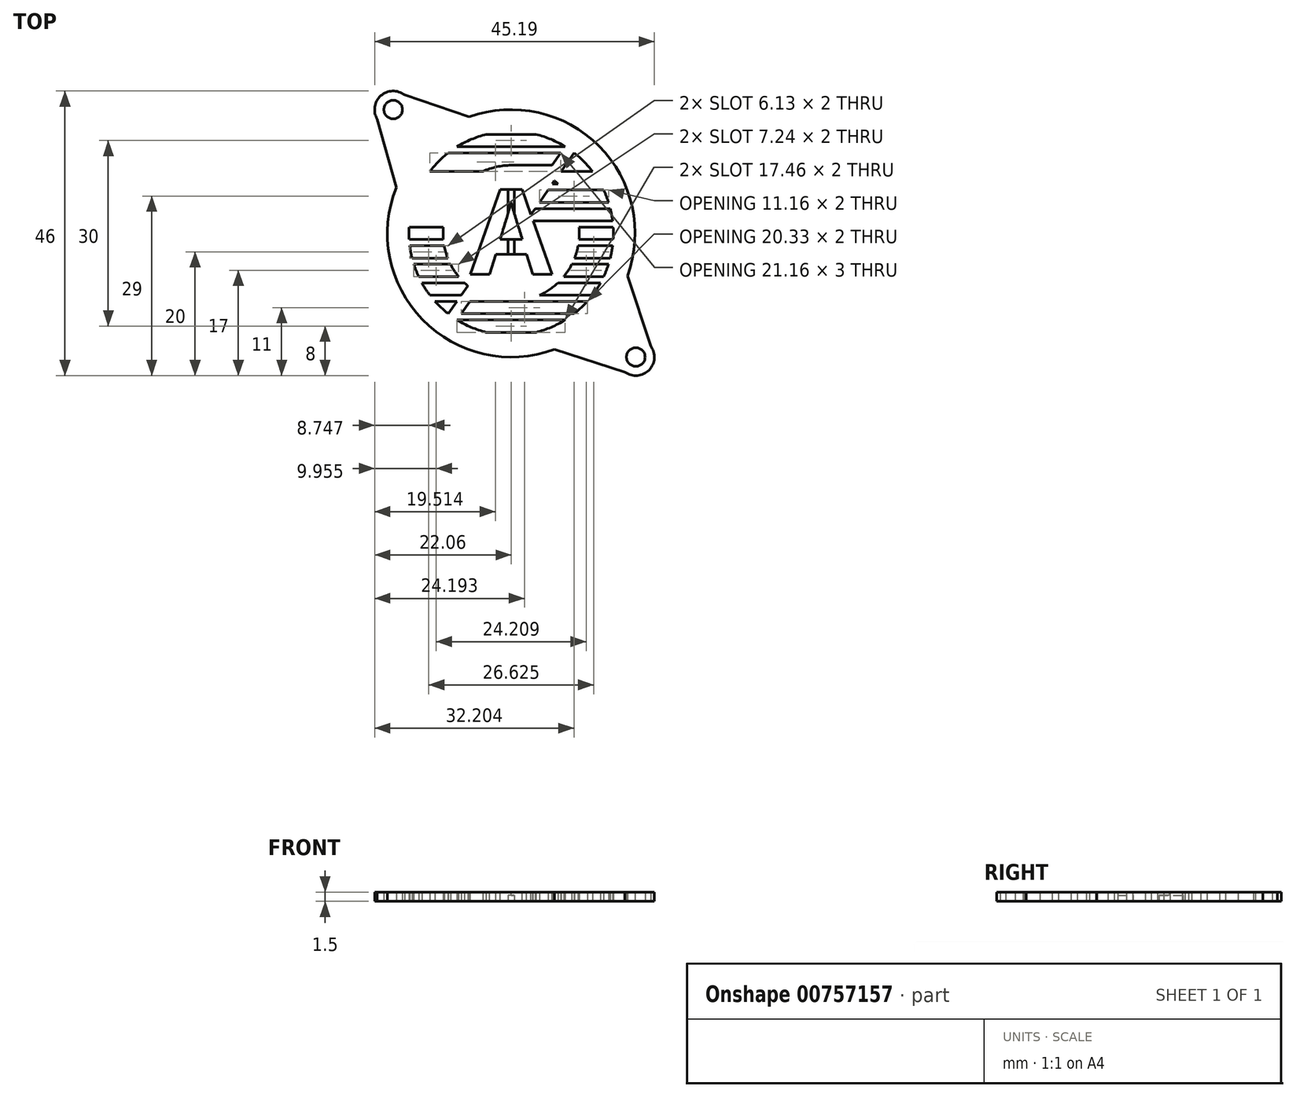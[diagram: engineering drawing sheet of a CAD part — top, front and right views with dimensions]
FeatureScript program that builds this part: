
annotation { "Feature Type Name" : "Feature", "Feature Type Description" : "" }
export const myFeature = defineFeature(function(context is Context, id is Id, definition is map)
    precondition{}
    {
        {
            var Q0;
            Q0=qCreatedBy(makeId("Top.planeOp"),FACE);
            var sketch = newSketch(context, id + "F0", { "sketchPlane" : qUnion([Q0])});
            skLineSegment(sketch, "E0", {"start": v(0, 0) * mm, "end": v(0, -20) * mm, "construction": true});
            skLineSegment(sketch, "E1", {"start": v(0, 0) * mm, "end": v(0, 20) * mm, "construction": true});
            skLineSegment(sketch, "E2", {"start": v(0, 20) * mm, "end": v(-19.06, 20) * mm, "construction": true});
            skLineSegment(sketch, "E3", {"start": v(0, -20) * mm, "end": v(20.13, -20) * mm, "construction": true});
            skCircle(sketch, "E4", {"center": v(-19.06, 20) * mm, "radius": 1.5 * mm});
            skCircle(sketch, "E5", {"center": v(20.13, -20) * mm, "radius": 1.5 * mm});
            skCircle(sketch, "E6", {"center": v(0, 0) * mm, "radius": 16.5 * mm});
            skArc(sketch, "E7", {"start": v(-17.23, 22.38) * mm, "mid": v(-21.06, 22.24) * mm, "end": v(-21.63, 18.45) * mm});
            skArc(sketch, "E8", {"start": v(18.38, -22.43) * mm, "mid": v(22.27, -22.1) * mm, "end": v(22.54, -18.2) * mm});
            skLineSegment(sketch, "E9", {"start": v(-19.06, 20) * mm, "end": v(-30.1, 20) * mm, "construction": true});
            skLineSegment(sketch, "E10", {"start": v(-19.06, 20) * mm, "end": v(-19.06, 32.46) * mm, "construction": true});
            skLineSegment(sketch, "E11", {"start": v(20.13, -20) * mm, "end": v(30, -20) * mm, "construction": true});
            skLineSegment(sketch, "E12", {"start": v(20.13, -20) * mm, "end": v(20.13, -30.36) * mm, "construction": true});
            skLineSegment(sketch, "E13", {"start": v(-21.63, 18.45) * mm, "end": v(-18.57, 7.43) * mm});
            skLineSegment(sketch, "E14", {"start": v(-17.23, 22.38) * mm, "end": v(-6.79, 18.81) * mm});
            skLineSegment(sketch, "E15", {"start": v(18.38, -22.43) * mm, "end": v(6.96, -18.75) * mm});
            skLineSegment(sketch, "E16", {"start": v(22.54, -18.2) * mm, "end": v(18.78, -6.88) * mm});
            skArc(sketch, "E17", {"start": v(-18.57, 7.43) * mm, "mid": v(-14.32, -13.96) * mm, "end": v(6.96, -18.75) * mm});
            skPoint(sketch, "E18.orphan", {"position": v(-16.5, 0) * mm});
            skPoint(sketch, "E19.orphan", {"position": v(16.5, 0) * mm});
            skArc(sketch, "E20.trimOffspring", {"start": v(18.78, -6.88) * mm, "mid": v(14.18, 14.1) * mm, "end": v(-6.79, 18.81) * mm});
            skLineSegment(sketch, "E21", {"start": v(-16.47, 1) * mm, "end": v(16.47, 1) * mm});
            skLineSegment(sketch, "E22", {"start": v(16.38, 2) * mm, "end": v(-16.38, 2) * mm});
            skLineSegment(sketch, "E23", {"start": v(-16, 4) * mm, "end": v(16, 4) * mm});
            skLineSegment(sketch, "E24", {"start": v(15.72, 5) * mm, "end": v(-15.72, 5) * mm});
            skLineSegment(sketch, "E25", {"start": v(-14.94, 7) * mm, "end": v(14.94, 7) * mm});
            skLineSegment(sketch, "E26", {"start": v(14.43, 8) * mm, "end": v(-14.43, 8) * mm});
            skLineSegment(sketch, "E27", {"start": v(-13.12, 10) * mm, "end": v(13.12, 10) * mm});
            skLineSegment(sketch, "E28", {"start": v(12.3, 11) * mm, "end": v(-12.3, 11) * mm});
            skLineSegment(sketch, "E29", {"start": v(-10.16, 13) * mm, "end": v(10.16, 13) * mm});
            skLineSegment(sketch, "E30", {"start": v(8.73, 14) * mm, "end": v(-8.73, 14) * mm});
            skLineSegment(sketch, "E31", {"start": v(-4.03, 16) * mm, "end": v(4.03, 16) * mm});
            skLineSegment(sketch, "E32.MirrorCS", {"start": v(-16.47, -1) * mm, "end": v(16.47, -1) * mm});
            skLineSegment(sketch, "E33.MirrorCS", {"start": v(16.38, -2) * mm, "end": v(-16.38, -2) * mm});
            skLineSegment(sketch, "E34.MirrorCS", {"start": v(-16, -4) * mm, "end": v(16, -4) * mm});
            skLineSegment(sketch, "E35.MirrorCS", {"start": v(15.72, -5) * mm, "end": v(-15.72, -5) * mm});
            skLineSegment(sketch, "E36.MirrorCS", {"start": v(-14.94, -7) * mm, "end": v(14.94, -7) * mm});
            skLineSegment(sketch, "E37.MirrorCS", {"start": v(14.43, -8) * mm, "end": v(-14.43, -8) * mm});
            skLineSegment(sketch, "E38.MirrorCS", {"start": v(-13.12, -10) * mm, "end": v(13.12, -10) * mm});
            skLineSegment(sketch, "E39.MirrorCS", {"start": v(12.3, -11) * mm, "end": v(-12.3, -11) * mm});
            skLineSegment(sketch, "E40.MirrorCS", {"start": v(-10.16, -13) * mm, "end": v(10.16, -13) * mm});
            skLineSegment(sketch, "E41.MirrorCS", {"start": v(-4.03, -16) * mm, "end": v(4.03, -16) * mm});
            skLineSegment(sketch, "E42.MirrorCS", {"start": v(8.73, -14) * mm, "end": v(-8.73, -14) * mm});
            skLineSegment(sketch, "E43", {"start": v(8.73, 14) * mm, "end": v(-10.16, -13) * mm});
            skLineSegment(sketch, "E44", {"start": v(-8.73, -14) * mm, "end": v(10.16, 13) * mm});
            skCircle(sketch, "E45", {"center": v(0, 0) * mm, "radius": 11 * mm});
            skSolve(sketch);
        }
        {
            var Q0;
            Q0=makeQuery(id+"F0.imprint","IMPRINT",FACE,{"disambiguationData":[TD([[makeQuery(id+"F0.imprint","IMPRINT",EDGE,{"derivedFrom":sQuery(id+"F0.wireOp",EDGE,"E4")}),-1.0]])]});
            extrude(context, id + "F1", {"entities" : qUnion([Q0]), "depth" : 1.5 * mm, "offsetDistance" : 25 * mm});
        }
        {
            var Q0;
            {var subQ0=sQuery(id+"F0.wireOp",EDGE,"E31");Q0=makeQuery(id+"F0.imprint","IMPRINT",FACE,{"disambiguationData":[TD([[makeQuery(id+"F0.imprint","IMPRINT",EDGE,{"derivedFrom":subQ0}),1.0]])]});}
            var Q1;
            {var subQ0=sQuery(id+"F0.wireOp",EDGE,"E29");Q1=makeQuery(id+"F0.imprint","IMPRINT",FACE,{"disambiguationData":[TD([[makeQuery(id+"F0.imprint","IMPRINT",EDGE,{"derivedFrom":subQ0}),1.0]])]});}
            var Q2;
            {var subQ0=sQuery(id+"F0.wireOp",EDGE,"E27");Q2=makeQuery(id+"F0.imprint","IMPRINT",FACE,{"disambiguationData":[TD([[makeQuery(id+"F0.imprint","IMPRINT",EDGE,{"derivedFrom":subQ0}),1.0]])]});}
            var Q3;
            {var subQ0=sQuery(id+"F0.wireOp",EDGE,"E25");Q3=makeQuery(id+"F0.imprint","IMPRINT",FACE,{"disambiguationData":[TD([[makeQuery(id+"F0.imprint","IMPRINT",EDGE,{"derivedFrom":subQ0}),1.0]])]});}
            var Q4;
            {var subQ0=sQuery(id+"F0.wireOp",EDGE,"E23");Q4=makeQuery(id+"F0.imprint","IMPRINT",FACE,{"disambiguationData":[TD([[makeQuery(id+"F0.imprint","IMPRINT",EDGE,{"derivedFrom":subQ0}),1.0]])]});}
            var Q5;
            {var subQ0=sQuery(id+"F0.wireOp",EDGE,"E21");Q5=makeQuery(id+"F0.imprint","IMPRINT",FACE,{"disambiguationData":[TD([[makeQuery(id+"F0.imprint","IMPRINT",EDGE,{"derivedFrom":subQ0}),1.0]])]});}
            var Q6;
            {var subQ0=sQuery(id+"F0.wireOp",EDGE,"E32.MirrorCS");Q6=makeQuery(id+"F0.imprint","IMPRINT",FACE,{"disambiguationData":[TD([[makeQuery(id+"F0.imprint","IMPRINT",EDGE,{"derivedFrom":subQ0}),-1.0]])]});}
            var Q7;
            {var subQ0=sQuery(id+"F0.wireOp",EDGE,"E34.MirrorCS");Q7=makeQuery(id+"F0.imprint","IMPRINT",FACE,{"disambiguationData":[TD([[makeQuery(id+"F0.imprint","IMPRINT",EDGE,{"derivedFrom":subQ0}),-1.0]])]});}
            var Q8;
            {var subQ0=sQuery(id+"F0.wireOp",EDGE,"E36.MirrorCS");Q8=makeQuery(id+"F0.imprint","IMPRINT",FACE,{"disambiguationData":[TD([[makeQuery(id+"F0.imprint","IMPRINT",EDGE,{"derivedFrom":subQ0}),-1.0]])]});}
            var Q9;
            {var subQ0=sQuery(id+"F0.wireOp",EDGE,"E38.MirrorCS");Q9=makeQuery(id+"F0.imprint","IMPRINT",FACE,{"disambiguationData":[TD([[makeQuery(id+"F0.imprint","IMPRINT",EDGE,{"derivedFrom":subQ0}),-1.0]])]});}
            var Q10;
            {var subQ0=sQuery(id+"F0.wireOp",EDGE,"E40.MirrorCS");Q10=makeQuery(id+"F0.imprint","IMPRINT",FACE,{"disambiguationData":[TD([[makeQuery(id+"F0.imprint","IMPRINT",EDGE,{"derivedFrom":subQ0}),-1.0]])]});}
            var Q11;
            {var subQ0=sQuery(id+"F0.wireOp",EDGE,"E41.MirrorCS");Q11=makeQuery(id+"F0.imprint","IMPRINT",FACE,{"disambiguationData":[TD([[makeQuery(id+"F0.imprint","IMPRINT",EDGE,{"derivedFrom":subQ0}),-1.0]])]});}
            var Q12;
            {var subQ3=sQuery(id+"F0.wireOp",EDGE,"E42.MirrorCS");Q12=makeQuery(id+"F0.imprint","IMPRINT",FACE,{"disambiguationData":[TD([[makeQuery(id+"F0.imprint","IMPRINT",EDGE,{"derivedFrom":subQ3}),-1.0]])]});}
            var Q13;
            {var subQ3=sQuery(id+"F0.wireOp",EDGE,"E30");Q13=makeQuery(id+"F0.imprint","IMPRINT",FACE,{"disambiguationData":[TD([[makeQuery(id+"F0.imprint","IMPRINT",EDGE,{"derivedFrom":subQ3}),1.0]])]});}
            var Q14;
            {var subQ0=sQuery(id+"F0.wireOp",EDGE,"E44");var subQ1=sQuery(id+"F0.wireOp",EDGE,"E39.MirrorCS");var subQ2=makeQuery(id+"F0.imprint","INTERSECT",VERTEX,{"derivedFrom":[subQ1,subQ0]});Q14=makeQuery(id+"F0.imprint","IMPRINT",FACE,{"disambiguationData":[TD([[makeQuery(id+"F0.imprint","IMPRINT",EDGE,{"disambiguationData":[TD([[subQ2,-1.0]])],"derivedFrom":subQ1}),1.0]])]});}
            var Q15;
            {var subQ0=sQuery(id+"F0.wireOp",EDGE,"E44");var subQ1=sQuery(id+"F0.wireOp",EDGE,"E37.MirrorCS");var subQ2=makeQuery(id+"F0.imprint","INTERSECT",VERTEX,{"derivedFrom":[subQ1,subQ0]});Q15=makeQuery(id+"F0.imprint","IMPRINT",FACE,{"disambiguationData":[TD([[makeQuery(id+"F0.imprint","IMPRINT",EDGE,{"disambiguationData":[TD([[subQ2,-1.0]])],"derivedFrom":subQ1}),1.0]])]});}
            var Q16;
            {var subQ0=sQuery(id+"F0.wireOp",EDGE,"E44");var subQ1=sQuery(id+"F0.wireOp",EDGE,"E35.MirrorCS");var subQ2=makeQuery(id+"F0.imprint","INTERSECT",VERTEX,{"derivedFrom":[subQ1,subQ0]});Q16=makeQuery(id+"F0.imprint","IMPRINT",FACE,{"disambiguationData":[TD([[makeQuery(id+"F0.imprint","IMPRINT",EDGE,{"disambiguationData":[TD([[subQ2,-1.0]])],"derivedFrom":subQ1}),1.0]])]});}
            var Q17;
            {var subQ0=sQuery(id+"F0.wireOp",EDGE,"E44");var subQ1=sQuery(id+"F0.wireOp",EDGE,"E33.MirrorCS");var subQ2=makeQuery(id+"F0.imprint","INTERSECT",VERTEX,{"derivedFrom":[subQ1,subQ0]});Q17=makeQuery(id+"F0.imprint","IMPRINT",FACE,{"disambiguationData":[TD([[makeQuery(id+"F0.imprint","IMPRINT",EDGE,{"disambiguationData":[TD([[subQ2,-1.0]])],"derivedFrom":subQ1}),1.0]])]});}
            var Q18;
            {var subQ0=sQuery(id+"F0.wireOp",EDGE,"E43");var subQ1=sQuery(id+"F0.wireOp",EDGE,"E21");var subQ2=makeQuery(id+"F0.imprint","INTERSECT",VERTEX,{"derivedFrom":[subQ1,subQ0]});Q18=makeQuery(id+"F0.imprint","IMPRINT",FACE,{"disambiguationData":[TD([[makeQuery(id+"F0.imprint","IMPRINT",EDGE,{"disambiguationData":[TD([[subQ2,-1.0]])],"derivedFrom":subQ1}),-1.0]])]});}
            var Q19;
            {var subQ0=sQuery(id+"F0.wireOp",EDGE,"E44");var subQ1=sQuery(id+"F0.wireOp",EDGE,"E22");var subQ2=makeQuery(id+"F0.imprint","INTERSECT",VERTEX,{"derivedFrom":[subQ1,subQ0]});Q19=makeQuery(id+"F0.imprint","IMPRINT",FACE,{"disambiguationData":[TD([[makeQuery(id+"F0.imprint","IMPRINT",EDGE,{"disambiguationData":[TD([[subQ2,-1.0]])],"derivedFrom":subQ1}),-1.0]])]});}
            var Q20;
            {var subQ0=sQuery(id+"F0.wireOp",EDGE,"E44");var subQ1=sQuery(id+"F0.wireOp",EDGE,"E24");var subQ2=makeQuery(id+"F0.imprint","INTERSECT",VERTEX,{"derivedFrom":[subQ1,subQ0]});Q20=makeQuery(id+"F0.imprint","IMPRINT",FACE,{"disambiguationData":[TD([[makeQuery(id+"F0.imprint","IMPRINT",EDGE,{"disambiguationData":[TD([[subQ2,-1.0]])],"derivedFrom":subQ1}),-1.0]])]});}
            var Q21;
            {var subQ0=sQuery(id+"F0.wireOp",EDGE,"E44");var subQ1=sQuery(id+"F0.wireOp",EDGE,"E26");var subQ2=makeQuery(id+"F0.imprint","INTERSECT",VERTEX,{"derivedFrom":[subQ1,subQ0]});Q21=makeQuery(id+"F0.imprint","IMPRINT",FACE,{"disambiguationData":[TD([[makeQuery(id+"F0.imprint","IMPRINT",EDGE,{"disambiguationData":[TD([[subQ2,-1.0]])],"derivedFrom":subQ1}),-1.0]])]});}
            var Q22;
            {var subQ0=sQuery(id+"F0.wireOp",EDGE,"E44");var subQ1=sQuery(id+"F0.wireOp",EDGE,"E28");var subQ2=makeQuery(id+"F0.imprint","INTERSECT",VERTEX,{"derivedFrom":[subQ1,subQ0]});Q22=makeQuery(id+"F0.imprint","IMPRINT",FACE,{"disambiguationData":[TD([[makeQuery(id+"F0.imprint","IMPRINT",EDGE,{"disambiguationData":[TD([[subQ2,-1.0]])],"derivedFrom":subQ1}),-1.0]])]});}
            var Q23;
            {var subQ0=sQuery(id+"F0.wireOp",EDGE,"E43");var subQ1=sQuery(id+"F0.wireOp",EDGE,"E26");var subQ2=makeQuery(id+"F0.imprint","INTERSECT",VERTEX,{"derivedFrom":[subQ1,subQ0]});Q23=makeQuery(id+"F0.imprint","IMPRINT",FACE,{"disambiguationData":[TD([[makeQuery(id+"F0.imprint","IMPRINT",EDGE,{"disambiguationData":[TD([[subQ2,-1.0]])],"derivedFrom":subQ1}),-1.0]])]});}
            var Q24;
            {var subQ0=sQuery(id+"F0.wireOp",EDGE,"E43");var subQ1=sQuery(id+"F0.wireOp",EDGE,"E24");var subQ2=makeQuery(id+"F0.imprint","INTERSECT",VERTEX,{"derivedFrom":[subQ1,subQ0]});Q24=makeQuery(id+"F0.imprint","IMPRINT",FACE,{"disambiguationData":[TD([[makeQuery(id+"F0.imprint","IMPRINT",EDGE,{"disambiguationData":[TD([[subQ2,-1.0]])],"derivedFrom":subQ1}),-1.0]])]});}
            var Q25;
            {var subQ0=sQuery(id+"F0.wireOp",EDGE,"E43");var subQ1=sQuery(id+"F0.wireOp",EDGE,"E27");var subQ2=makeQuery(id+"F0.imprint","INTERSECT",VERTEX,{"derivedFrom":[subQ1,subQ0]});Q25=makeQuery(id+"F0.imprint","IMPRINT",FACE,{"disambiguationData":[TD([[makeQuery(id+"F0.imprint","IMPRINT",EDGE,{"disambiguationData":[TD([[subQ2,-1.0]])],"derivedFrom":subQ1}),-1.0]])]});}
            var Q26;
            {var subQ0=sQuery(id+"F0.wireOp",EDGE,"E43");var subQ1=sQuery(id+"F0.wireOp",EDGE,"E27");var subQ2=makeQuery(id+"F0.imprint","INTERSECT",VERTEX,{"derivedFrom":[subQ1,subQ0]});Q26=makeQuery(id+"F0.imprint","IMPRINT",FACE,{"disambiguationData":[TD([[makeQuery(id+"F0.imprint","IMPRINT",EDGE,{"disambiguationData":[TD([[subQ2,-1.0]])],"derivedFrom":subQ1}),1.0]])]});}
            var Q27;
            {var subQ0=sQuery(id+"F0.wireOp",EDGE,"E45");var subQ1=sQuery(id+"F0.wireOp",EDGE,"E27");var subQ2=makeQuery(id+"F0.imprint","INTERSECT",VERTEX,{"disambiguationData":[OD(1.0)],"derivedFrom":[subQ1,subQ0]});Q27=makeQuery(id+"F0.imprint","IMPRINT",FACE,{"disambiguationData":[TD([[makeQuery(id+"F0.imprint","IMPRINT",EDGE,{"disambiguationData":[TD([[subQ2,-1.0]])],"derivedFrom":subQ1}),1.0]])]});}
            var Q28;
            {var subQ0=sQuery(id+"F0.wireOp",EDGE,"E27");var subQ1=sQuery(id+"F0.wireOp",EDGE,"E6");var subQ2=makeQuery(id+"F0.imprint","INTERSECT",VERTEX,{"disambiguationData":[OD(1.0)],"derivedFrom":[subQ1,subQ0]});Q28=makeQuery(id+"F0.imprint","IMPRINT",FACE,{"disambiguationData":[TD([[makeQuery(id+"F0.imprint","IMPRINT",EDGE,{"disambiguationData":[TD([[subQ2,-1.0]])],"derivedFrom":subQ1}),1.0]])]});}
            var Q29;
            {var subQ0=sQuery(id+"F0.wireOp",EDGE,"E27");var subQ1=sQuery(id+"F0.wireOp",EDGE,"E6");var subQ2=makeQuery(id+"F0.imprint","INTERSECT",VERTEX,{"disambiguationData":[OD(0.0)],"derivedFrom":[subQ1,subQ0]});Q29=makeQuery(id+"F0.imprint","IMPRINT",FACE,{"disambiguationData":[TD([[makeQuery(id+"F0.imprint","IMPRINT",EDGE,{"disambiguationData":[TD([[subQ2,1.0]])],"derivedFrom":subQ1}),1.0]])]});}
            var Q30;
            {var subQ0=sQuery(id+"F0.wireOp",EDGE,"E38.MirrorCS");var subQ1=sQuery(id+"F0.wireOp",EDGE,"E6");var subQ2=makeQuery(id+"F0.imprint","INTERSECT",VERTEX,{"disambiguationData":[OD(0.0)],"derivedFrom":[subQ1,subQ0]});Q30=makeQuery(id+"F0.imprint","IMPRINT",FACE,{"disambiguationData":[TD([[makeQuery(id+"F0.imprint","IMPRINT",EDGE,{"disambiguationData":[TD([[subQ2,-1.0]])],"derivedFrom":subQ1}),1.0]])]});}
            var Q31;
            {var subQ0=sQuery(id+"F0.wireOp",EDGE,"E43");var subQ1=sQuery(id+"F0.wireOp",EDGE,"E38.MirrorCS");var subQ2=makeQuery(id+"F0.imprint","INTERSECT",VERTEX,{"derivedFrom":[subQ1,subQ0]});Q31=makeQuery(id+"F0.imprint","IMPRINT",FACE,{"disambiguationData":[TD([[makeQuery(id+"F0.imprint","IMPRINT",EDGE,{"disambiguationData":[TD([[subQ2,-1.0]])],"derivedFrom":subQ1}),-1.0]])]});}
            var Q32;
            {var subQ0=sQuery(id+"F0.wireOp",EDGE,"E43");var subQ1=sQuery(id+"F0.wireOp",EDGE,"E38.MirrorCS");var subQ2=makeQuery(id+"F0.imprint","INTERSECT",VERTEX,{"derivedFrom":[subQ1,subQ0]});Q32=makeQuery(id+"F0.imprint","IMPRINT",FACE,{"disambiguationData":[TD([[makeQuery(id+"F0.imprint","IMPRINT",EDGE,{"disambiguationData":[TD([[subQ2,-1.0]])],"derivedFrom":subQ1}),1.0]])]});}
            var Q33;
            {var subQ0=sQuery(id+"F0.wireOp",EDGE,"E44");var subQ1=sQuery(id+"F0.wireOp",EDGE,"E38.MirrorCS");var subQ2=makeQuery(id+"F0.imprint","INTERSECT",VERTEX,{"derivedFrom":[subQ1,subQ0]});Q33=makeQuery(id+"F0.imprint","IMPRINT",FACE,{"disambiguationData":[TD([[makeQuery(id+"F0.imprint","IMPRINT",EDGE,{"disambiguationData":[TD([[subQ2,-1.0]])],"derivedFrom":subQ1}),-1.0]])]});}
            var Q34;
            {var subQ0=sQuery(id+"F0.wireOp",EDGE,"E38.MirrorCS");var subQ1=sQuery(id+"F0.wireOp",EDGE,"E6");var subQ2=makeQuery(id+"F0.imprint","INTERSECT",VERTEX,{"disambiguationData":[OD(1.0)],"derivedFrom":[subQ1,subQ0]});Q34=makeQuery(id+"F0.imprint","IMPRINT",FACE,{"disambiguationData":[TD([[makeQuery(id+"F0.imprint","IMPRINT",EDGE,{"disambiguationData":[TD([[subQ2,1.0]])],"derivedFrom":subQ1}),1.0]])]});}
            var Q35;
            {var subQ0=sQuery(id+"F0.wireOp",EDGE,"E45");var subQ5=sQuery(id+"F0.wireOp",EDGE,"E37.MirrorCS");var subQ8=makeQuery(id+"F0.imprint","INTERSECT",VERTEX,{"disambiguationData":[OD(0.0)],"derivedFrom":[subQ5,subQ0]});Q35=makeQuery(id+"F0.imprint","IMPRINT",FACE,{"disambiguationData":[TD([[makeQuery(id+"F0.imprint","IMPRINT",EDGE,{"disambiguationData":[TD([[subQ8,-1.0]])],"derivedFrom":subQ5}),1.0]])]});}
            var Q36;
            {var subQ0=sQuery(id+"F0.wireOp",EDGE,"E45");var subQ1=sQuery(id+"F0.wireOp",EDGE,"E35.MirrorCS");var subQ2=makeQuery(id+"F0.imprint","INTERSECT",VERTEX,{"disambiguationData":[OD(0.0)],"derivedFrom":[subQ1,subQ0]});Q36=makeQuery(id+"F0.imprint","IMPRINT",FACE,{"disambiguationData":[TD([[makeQuery(id+"F0.imprint","IMPRINT",EDGE,{"disambiguationData":[TD([[subQ2,-1.0]])],"derivedFrom":subQ1}),1.0]])]});}
            var Q37;
            {var subQ0=sQuery(id+"F0.wireOp",EDGE,"E45");var subQ1=sQuery(id+"F0.wireOp",EDGE,"E33.MirrorCS");var subQ2=makeQuery(id+"F0.imprint","INTERSECT",VERTEX,{"disambiguationData":[OD(0.0)],"derivedFrom":[subQ1,subQ0]});Q37=makeQuery(id+"F0.imprint","IMPRINT",FACE,{"disambiguationData":[TD([[makeQuery(id+"F0.imprint","IMPRINT",EDGE,{"disambiguationData":[TD([[subQ2,-1.0]])],"derivedFrom":subQ1}),1.0]])]});}
            var Q38;
            {var subQ0=sQuery(id+"F0.wireOp",EDGE,"E44");var subQ1=sQuery(id+"F0.wireOp",EDGE,"E21");var subQ2=makeQuery(id+"F0.imprint","INTERSECT",VERTEX,{"derivedFrom":[subQ1,subQ0]});Q38=makeQuery(id+"F0.imprint","IMPRINT",FACE,{"disambiguationData":[TD([[makeQuery(id+"F0.imprint","IMPRINT",EDGE,{"disambiguationData":[TD([[subQ2,-1.0]])],"derivedFrom":subQ1}),-1.0]])]});}
            var Q39;
            {var subQ0=sQuery(id+"F0.wireOp",EDGE,"E45");var subQ1=sQuery(id+"F0.wireOp",EDGE,"E22");var subQ2=makeQuery(id+"F0.imprint","INTERSECT",VERTEX,{"disambiguationData":[OD(0.0)],"derivedFrom":[subQ1,subQ0]});Q39=makeQuery(id+"F0.imprint","IMPRINT",FACE,{"disambiguationData":[TD([[makeQuery(id+"F0.imprint","IMPRINT",EDGE,{"disambiguationData":[TD([[subQ2,-1.0]])],"derivedFrom":subQ1}),-1.0]])]});}
            var Q40;
            {var subQ0=sQuery(id+"F0.wireOp",EDGE,"E45");var subQ1=sQuery(id+"F0.wireOp",EDGE,"E24");var subQ2=makeQuery(id+"F0.imprint","INTERSECT",VERTEX,{"disambiguationData":[OD(0.0)],"derivedFrom":[subQ1,subQ0]});Q40=makeQuery(id+"F0.imprint","IMPRINT",FACE,{"disambiguationData":[TD([[makeQuery(id+"F0.imprint","IMPRINT",EDGE,{"disambiguationData":[TD([[subQ2,-1.0]])],"derivedFrom":subQ1}),-1.0]])]});}
            var Q41;
            {var subQ0=sQuery(id+"F0.wireOp",EDGE,"E43");var subQ1=sQuery(id+"F0.wireOp",EDGE,"E22");var subQ2=makeQuery(id+"F0.imprint","INTERSECT",VERTEX,{"derivedFrom":[subQ1,subQ0]});Q41=makeQuery(id+"F0.imprint","IMPRINT",FACE,{"disambiguationData":[TD([[makeQuery(id+"F0.imprint","IMPRINT",EDGE,{"disambiguationData":[TD([[subQ2,-1.0]])],"derivedFrom":subQ1}),-1.0]])]});}
            var Q42;
            {var subQ0=sQuery(id+"F0.wireOp",EDGE,"E45");var subQ1=sQuery(id+"F0.wireOp",EDGE,"E21");var subQ2=makeQuery(id+"F0.imprint","INTERSECT",VERTEX,{"disambiguationData":[OD(0.0)],"derivedFrom":[subQ1,subQ0]});Q42=makeQuery(id+"F0.imprint","IMPRINT",FACE,{"disambiguationData":[TD([[makeQuery(id+"F0.imprint","IMPRINT",EDGE,{"disambiguationData":[TD([[subQ2,-1.0]])],"derivedFrom":subQ1}),-1.0]])]});}
            var Q43;
            {var subQ0=sQuery(id+"F0.wireOp",EDGE,"E43");var subQ1=sQuery(id+"F0.wireOp",EDGE,"E33.MirrorCS");var subQ2=makeQuery(id+"F0.imprint","INTERSECT",VERTEX,{"derivedFrom":[subQ1,subQ0]});Q43=makeQuery(id+"F0.imprint","IMPRINT",FACE,{"disambiguationData":[TD([[makeQuery(id+"F0.imprint","IMPRINT",EDGE,{"disambiguationData":[TD([[subQ2,-1.0]])],"derivedFrom":subQ1}),1.0]])]});}
            var Q44;
            {var subQ0=sQuery(id+"F0.wireOp",EDGE,"E43");var subQ1=sQuery(id+"F0.wireOp",EDGE,"E35.MirrorCS");var subQ2=makeQuery(id+"F0.imprint","INTERSECT",VERTEX,{"derivedFrom":[subQ1,subQ0]});Q44=makeQuery(id+"F0.imprint","IMPRINT",FACE,{"disambiguationData":[TD([[makeQuery(id+"F0.imprint","IMPRINT",EDGE,{"disambiguationData":[TD([[subQ2,-1.0]])],"derivedFrom":subQ1}),1.0]])]});}
            var Q45;
            {var subQ0=sQuery(id+"F0.wireOp",EDGE,"E45");var subQ1=sQuery(id+"F0.wireOp",EDGE,"E27");var subQ2=makeQuery(id+"F0.imprint","INTERSECT",VERTEX,{"disambiguationData":[OD(1.0)],"derivedFrom":[subQ1,subQ0]});Q45=makeQuery(id+"F0.imprint","IMPRINT",FACE,{"disambiguationData":[TD([[makeQuery(id+"F0.imprint","IMPRINT",EDGE,{"disambiguationData":[TD([[subQ2,-1.0]])],"derivedFrom":subQ1}),-1.0]])]});}
            var Q46;
            {var subQ0=sQuery(id+"F0.wireOp",EDGE,"E44");var subQ1=sQuery(id+"F0.wireOp",EDGE,"E38.MirrorCS");var subQ2=makeQuery(id+"F0.imprint","INTERSECT",VERTEX,{"derivedFrom":[subQ1,subQ0]});Q46=makeQuery(id+"F0.imprint","IMPRINT",FACE,{"disambiguationData":[TD([[makeQuery(id+"F0.imprint","IMPRINT",EDGE,{"disambiguationData":[TD([[subQ2,-1.0]])],"derivedFrom":subQ1}),1.0]])]});}
            var Q47;
            {var subQ0=sQuery(id+"F0.wireOp",EDGE,"E43");var subQ1=sQuery(id+"F0.wireOp",EDGE,"E37.MirrorCS");var subQ2=makeQuery(id+"F0.imprint","INTERSECT",VERTEX,{"derivedFrom":[subQ1,subQ0]});Q47=makeQuery(id+"F0.imprint","IMPRINT",FACE,{"disambiguationData":[TD([[makeQuery(id+"F0.imprint","IMPRINT",EDGE,{"disambiguationData":[TD([[subQ2,-1.0]])],"derivedFrom":subQ1}),1.0]])]});}
            var Q48;
            {var subQ0=sQuery(id+"F0.wireOp",EDGE,"E45");var subQ1=sQuery(id+"F0.wireOp",EDGE,"E26");var subQ2=makeQuery(id+"F0.imprint","INTERSECT",VERTEX,{"disambiguationData":[OD(0.0)],"derivedFrom":[subQ1,subQ0]});Q48=makeQuery(id+"F0.imprint","IMPRINT",FACE,{"disambiguationData":[TD([[makeQuery(id+"F0.imprint","IMPRINT",EDGE,{"disambiguationData":[TD([[subQ2,-1.0]])],"derivedFrom":subQ1}),-1.0]])]});}
            extrude(context, id + "F2", {"entities" : qUnion([Q0, Q1, Q2, Q3, Q4, Q5, Q6, Q7, Q8, Q9, Q10, Q11, Q12, Q13, Q14, Q15, Q16, Q17, Q18, Q19, Q20, Q21, Q22, Q23, Q24, Q25, Q26, Q27, Q28, Q29, Q30, Q31, Q32, Q33, Q34, Q35, Q36, Q37, Q38, Q39, Q40, Q41, Q42, Q43, Q44, Q45, Q46, Q47, Q48]), "operationType" : NewBodyOperationType.ADD, "depth" : 1.5 * mm, "offsetDistance" : 25 * mm});
        }
        {
            var Q0;
            {var subQ0=sQuery(id+"F0.wireOp",EDGE,"E6");Q0=makeQuery(id+"F2.boolean.opBoolean","MERGE",FACE,{"derivedFrom":[makeQuery(id+"F1.opExtrude","CAP_FACE",FACE,{"disambiguationData":[OSD([sQuery(id+"F0.wireOp",EDGE,"E4"),sQuery(id+"F0.wireOp",EDGE,"E5"),subQ0,sQuery(id+"F0.wireOp",EDGE,"E7"),sQuery(id+"F0.wireOp",EDGE,"E8"),sQuery(id+"F0.wireOp",EDGE,"E13"),sQuery(id+"F0.wireOp",EDGE,"E14"),sQuery(id+"F0.wireOp",EDGE,"E15"),sQuery(id+"F0.wireOp",EDGE,"E16"),sQuery(id+"F0.wireOp",EDGE,"E17"),sQuery(id+"F0.wireOp",EDGE,"E20.trimOffspring")])],"isStart":false}),makeQuery(id+"F2.opExtrude","CAP_FACE",FACE,{"disambiguationData":[OSD([subQ0,sQuery(id+"F0.wireOp",EDGE,"E21"),sQuery(id+"F0.wireOp",EDGE,"E22"),sQuery(id+"F0.wireOp",EDGE,"E23"),sQuery(id+"F0.wireOp",EDGE,"E24"),sQuery(id+"F0.wireOp",EDGE,"E25"),sQuery(id+"F0.wireOp",EDGE,"E26"),sQuery(id+"F0.wireOp",EDGE,"E27"),sQuery(id+"F0.wireOp",EDGE,"E28"),sQuery(id+"F0.wireOp",EDGE,"E29"),sQuery(id+"F0.wireOp",EDGE,"E30"),sQuery(id+"F0.wireOp",EDGE,"E32.MirrorCS"),sQuery(id+"F0.wireOp",EDGE,"E33.MirrorCS"),sQuery(id+"F0.wireOp",EDGE,"E34.MirrorCS"),sQuery(id+"F0.wireOp",EDGE,"E35.MirrorCS"),sQuery(id+"F0.wireOp",EDGE,"E36.MirrorCS"),sQuery(id+"F0.wireOp",EDGE,"E37.MirrorCS"),sQuery(id+"F0.wireOp",EDGE,"E38.MirrorCS"),sQuery(id+"F0.wireOp",EDGE,"E39.MirrorCS"),sQuery(id+"F0.wireOp",EDGE,"E40.MirrorCS"),sQuery(id+"F0.wireOp",EDGE,"E42.MirrorCS"),sQuery(id+"F0.wireOp",EDGE,"E43"),sQuery(id+"F0.wireOp",EDGE,"E44"),sQuery(id+"F0.wireOp",EDGE,"E45")])],"isStart":false}),makeQuery(id+"F2.opExtrude","CAP_FACE",FACE,{"disambiguationData":[OSD([subQ0,sQuery(id+"F0.wireOp",EDGE,"E31")])],"isStart":false}),makeQuery(id+"F2.opExtrude","CAP_FACE",FACE,{"disambiguationData":[OSD([subQ0,sQuery(id+"F0.wireOp",EDGE,"E41.MirrorCS")])],"isStart":false})]});}
            var sketch = newSketch(context, id + "F3", { "sketchPlane" : qUnion([Q0])});
            skText(sketch, "E46", { "text": "A", "fontName": "OpenSans-Bold.ttf"});
            const initialGuessF3  = {"E46": [-0.00662, -0.00664, 1, 0, 0.0138]};
            skSetInitialGuess(sketch, initialGuessF3);
            skSolve(sketch);
        }
        {
            var Q0;
            Q0=makeQuery(id+"F3.imprint","IMPRINT",FACE,{"disambiguationData":[TD([[makeQuery(id+"F3.imprint","IMPRINT",EDGE,{"derivedFrom":sQuery(id+"F3.wireOp",EDGE,"E46.sketch_text.stroke-0")}),-1.0]])]});
            extrude(context, id + "F4", {"entities" : qUnion([Q0]), "operationType" : NewBodyOperationType.REMOVE, "oppositeDirection" : true, "depth" : 25 * mm, "offsetDistance" : 25 * mm});
        }
        {
            var Q0;
            Q0=qCreatedBy(makeId("Top.planeOp"),FACE);
            var sketch = newSketch(context, id + "F5", { "sketchPlane" : qUnion([Q0])});
            skLineSegment(sketch, "E47", {"start": v(0, -3.7) * mm, "end": v(-0.5, -3.7) * mm});
            skLineSegment(sketch, "E48", {"start": v(-0.5, -3.7) * mm, "end": v(-0.5, 7.68) * mm});
            skLineSegment(sketch, "E49", {"start": v(0, 7.68) * mm, "end": v(-0.5, 7.68) * mm});
            skLineSegment(sketch, "E50.MirrorCS", {"start": v(0, 7.68) * mm, "end": v(0.5, 7.68) * mm});
            skLineSegment(sketch, "E51.MirrorCS", {"start": v(0.5, -3.7) * mm, "end": v(0.5, 7.68) * mm});
            skLineSegment(sketch, "E52.MirrorCS", {"start": v(0, -3.7) * mm, "end": v(0.5, -3.7) * mm});
            skSolve(sketch);
        }
        {
            var Q0;
            Q0=makeQuery(id+"F5.imprint","IMPRINT",FACE,{"disambiguationData":[TD([[makeQuery(id+"F5.imprint","IMPRINT",EDGE,{"derivedFrom":sQuery(id+"F5.wireOp",EDGE,"E47")}),-1.0]])]});
            extrude(context, id + "F6", {"entities" : qUnion([Q0]), "operationType" : NewBodyOperationType.ADD, "depth" : 1 * mm, "offsetDistance" : 25 * mm});
        }
    });
